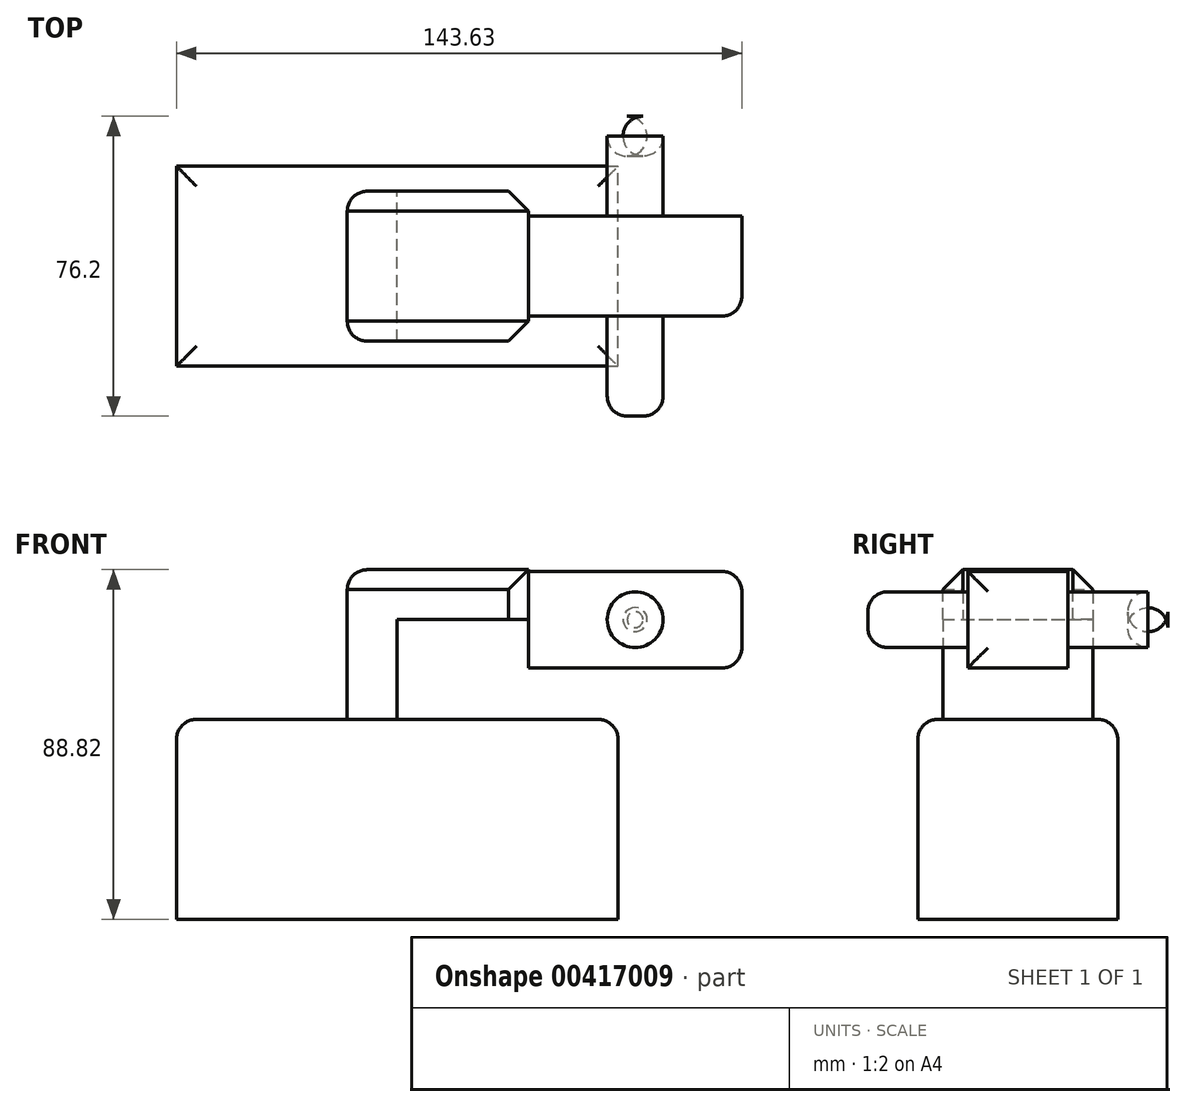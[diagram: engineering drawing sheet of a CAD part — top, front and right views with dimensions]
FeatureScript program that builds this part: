
annotation { "Feature Type Name" : "Feature", "Feature Type Description" : "" }
export const myFeature = defineFeature(function(context is Context, id is Id, definition is map)
    precondition{}
    {
        {
            var Q0;
            Q0=qCreatedBy(makeId("Front.planeOp"),FACE);
            var sketch = newSketch(context, id + "F0", { "sketchPlane" : qUnion([Q0])});
            skLineSegment(sketch, "E0.bottom", {"start": v(-40.66, 7.33) * mm, "end": v(71.52, 7.33) * mm});
            skLineSegment(sketch, "E0.top", {"start": v(-40.66, -43.47) * mm, "end": v(71.52, -43.47) * mm});
            skLineSegment(sketch, "E0.left", {"start": v(-40.66, 7.33) * mm, "end": v(-40.66, -43.47) * mm});
            skLineSegment(sketch, "E0.right", {"start": v(71.52, 7.33) * mm, "end": v(71.52, -43.47) * mm});
            skLineSegment(sketch, "E1.bottom", {"start": v(48.76, 44.92) * mm, "end": v(102.97, 44.92) * mm});
            skLineSegment(sketch, "E1.top", {"start": v(48.76, 20.37) * mm, "end": v(102.97, 20.37) * mm});
            skLineSegment(sketch, "E1.left", {"start": v(48.76, 44.92) * mm, "end": v(48.76, 20.37) * mm});
            skLineSegment(sketch, "E1.right", {"start": v(102.97, 44.92) * mm, "end": v(102.97, 20.37) * mm});
            skLineSegment(sketch, "E2", {"start": v(48.76, 32.65) * mm, "end": v(15.43, 32.65) * mm});
            skPoint(sketch, "E2.endSnap0", {"position": v(15.43, 7.33) * mm});
            skLineSegment(sketch, "E3", {"start": v(15.43, 32.65) * mm, "end": v(15.43, 7.33) * mm});
            skLineSegment(sketch, "E4.0", {"start": v(2.73, 45.35) * mm, "end": v(2.73, 7.33) * mm});
            skLineSegment(sketch, "E4.1", {"start": v(48.76, 45.35) * mm, "end": v(2.73, 45.35) * mm});
            skCircle(sketch, "E5", {"center": v(75.86, 32.65) * mm, "radius": 7.09 * mm});
            skPoint(sketch, "E5.centerSnap0", {"position": v(102.97, 32.65) * mm});
            skPoint(sketch, "E5.centerSnap1", {"position": v(75.86, 44.92) * mm});
            skLineSegment(sketch, "E6", {"start": v(2.73, 7.33) * mm, "end": v(15.43, 7.33) * mm});
            skLineSegment(sketch, "E7", {"start": v(48.76, 45.35) * mm, "end": v(48.76, 32.65) * mm});
            skSolve(sketch);
        }
        {
            var Q0;
            Q0=makeQuery(id+"F0.imprint","IMPRINT",FACE,{"disambiguationData":[TD([[makeQuery(id+"F0.imprint","IMPRINT",EDGE,{"derivedFrom":sQuery(id+"F0.wireOp",EDGE,"E0.top")}),1.0]])]});
            extrude(context, id + "F1", {"entities" : qUnion([Q0]), "endBound" : BoundingType.SYMMETRIC, "depth" : 50.8 * mm});
        }
        {
            var Q0;
            {var subQ3=sQuery(id+"F0.wireOp",EDGE,"E1.bottom");Q0=makeQuery(id+"F0.imprint","IMPRINT",FACE,{"disambiguationData":[TD([[makeQuery(id+"F0.imprint","IMPRINT",EDGE,{"derivedFrom":subQ3}),-1.0]])]});}
            extrude(context, id + "F2", {"entities" : qUnion([Q0]), "endBound" : BoundingType.SYMMETRIC, "depth" : 25.4 * mm});
        }
        {
            var Q0;
            Q0=makeQuery(id+"F0.imprint","IMPRINT",FACE,{"disambiguationData":[TD([[makeQuery(id+"F0.imprint","IMPRINT",EDGE,{"derivedFrom":sQuery(id+"F0.wireOp",EDGE,"E5")}),1.0]])]});
            extrude(context, id + "F3", {"entities" : qUnion([Q0]), "operationType" : NewBodyOperationType.ADD, "endBound" : BoundingType.SYMMETRIC, "depth" : 76.2 * mm});
        }
        {
            var Q0;
            {var subQ1=sQuery(id+"F0.wireOp",EDGE,"E2");Q0=makeQuery(id+"F0.imprint","IMPRINT",FACE,{"disambiguationData":[TD([[makeQuery(id+"F0.imprint","IMPRINT",EDGE,{"derivedFrom":subQ1}),-1.0]])]});}
            extrude(context, id + "F4", {"entities" : qUnion([Q0]), "endBound" : BoundingType.SYMMETRIC, "depth" : 38.1 * mm});
        }
        {
            var Q0;
            Q0=makeQuery(id+"F1.opExtrude","CAP_EDGE",EDGE,{"disambiguationData":[OSD([sQuery(id+"F0.wireOp",EDGE,"E0.bottom"),sQuery(id+"F0.wireOp",EDGE,"E6")])],"isStart":false});
            var Q1;
            Q1=makeQuery(id+"F1.opExtrude","SWEPT_EDGE",EDGE,{"disambiguationData":[OSD([sQuery(id+"F0.wireOp",EDGE,"E0.bottom"),sQuery(id+"F0.wireOp",EDGE,"E0.left")])]});
            var Q2;
            Q2=makeQuery(id+"F1.opExtrude","CAP_EDGE",EDGE,{"disambiguationData":[OSD([sQuery(id+"F0.wireOp",EDGE,"E0.bottom"),sQuery(id+"F0.wireOp",EDGE,"E6")])],"isStart":true});
            var Q3;
            Q3=makeQuery(id+"F1.opExtrude","SWEPT_EDGE",EDGE,{"disambiguationData":[OSD([sQuery(id+"F0.wireOp",EDGE,"E0.bottom"),sQuery(id+"F0.wireOp",EDGE,"E0.right")])]});
            var Q4;
            Q4=makeQuery(id+"F3.opExtrude","CAP_EDGE",EDGE,{"disambiguationData":[OSD([sQuery(id+"F0.wireOp",EDGE,"E5")])],"isStart":false});
            var Q5;
            Q5=makeQuery(id+"F3.opExtrude","CAP_EDGE",EDGE,{"disambiguationData":[OSD([sQuery(id+"F0.wireOp",EDGE,"E5")])],"isStart":true});
            fillet(context, id + "F5", {"entities" : qUnion([Q0, Q1, Q2, Q3, Q4, Q5]), "radius" : 5.08 * mm, "tangentPropagation" : true, "allowEdgeOverflow" : false});
        }
        {
            var Q0;
            Q0=makeQuery(id+"F2.opExtrude","SWEPT_EDGE",EDGE,{"disambiguationData":[OSD([sQuery(id+"F0.wireOp",EDGE,"E1.bottom"),sQuery(id+"F0.wireOp",EDGE,"E1.right")])]});
            var Q1;
            Q1=makeQuery(id+"F2.opExtrude","CAP_EDGE",EDGE,{"disambiguationData":[OSD([sQuery(id+"F0.wireOp",EDGE,"E1.right")])],"isStart":false});
            var Q2;
            Q2=makeQuery(id+"F2.opExtrude","SWEPT_EDGE",EDGE,{"disambiguationData":[OSD([sQuery(id+"F0.wireOp",EDGE,"E1.top"),sQuery(id+"F0.wireOp",EDGE,"E1.right")])]});
            var Q3;
            Q3=makeQuery(id+"F4.opExtrude","CAP_EDGE",EDGE,{"disambiguationData":[OSD([sQuery(id+"F0.wireOp",EDGE,"E4.0")])],"isStart":false});
            var Q4;
            Q4=makeQuery(id+"F4.opExtrude","SWEPT_EDGE",EDGE,{"disambiguationData":[OSD([sQuery(id+"F0.wireOp",EDGE,"E4.0"),sQuery(id+"F0.wireOp",EDGE,"E4.1")])]});
            var Q5;
            Q5=makeQuery(id+"F4.opExtrude","CAP_EDGE",EDGE,{"disambiguationData":[OSD([sQuery(id+"F0.wireOp",EDGE,"E4.0")])],"isStart":true});
            fillet(context, id + "F6", {"entities" : qUnion([Q0, Q1, Q2, Q3, Q4, Q5]), "radius" : 5.08 * mm, "tangentPropagation" : true, "allowEdgeOverflow" : false});
        }
        {
            var Q0;
            Q0=makeQuery(id+"F4.opExtrude","CAP_EDGE",EDGE,{"disambiguationData":[OSD([sQuery(id+"F0.wireOp",EDGE,"E4.1")])],"isStart":false});
            var Q1;
            Q1=makeQuery(id+"F4.opExtrude","CAP_EDGE",EDGE,{"disambiguationData":[OSD([sQuery(id+"F0.wireOp",EDGE,"E4.1")])],"isStart":true});
            var Q2;
            Q2=makeQuery(id+"F4.opExtrude","CAP_EDGE",EDGE,{"disambiguationData":[OSD([sQuery(id+"F0.wireOp",EDGE,"E7")])],"isStart":false});
            var Q3;
            Q3=makeQuery(id+"F4.opExtrude","CAP_EDGE",EDGE,{"disambiguationData":[OSD([sQuery(id+"F0.wireOp",EDGE,"E7")])],"isStart":true});
            chamfer(context, id + "F7", {"entities" : qUnion([Q0, Q1, Q2, Q3]), "width" : 5.08 * mm, "tangentPropagation" : true});
        }
    });
